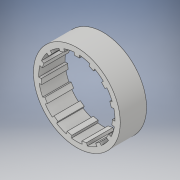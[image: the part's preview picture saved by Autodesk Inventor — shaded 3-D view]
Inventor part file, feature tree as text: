
AUTODESK INVENTOR PART (.ipt)
format: ipt  version: 2018 (Build 220112000, 112)  size: 170,496 bytes
history: native  units: in
note: dims shown in document units (in); Inventor stores cm internally (conversion verified against a paired STEP export)
features: extrude x2, sketch x1, pattern_circular x1
ambient origin geometry x8: Origin, YZ Plane, XZ Plane, XY Plane, X Axis, Y Axis, Z Axis, Center Point
bodies: Solid1 (feature_tree)
feature tree (4):
  sketch  "Sketch1"  dims[d0=1.65in d2=0.05in d3=0.1in d4=0.0275in d5=0.0275in d6=0.5in d7=0.0in d8=0.5in d9=0.0in d10=5.9055in d11=360.0deg]
  extrude  "Extrusion1"  Depth=0.5in
  extrude  "Extrusion2"  Depth=0.5in
  pattern_circular  "Circular Pattern1"  [2 undecoded]
note: 2 required parameter values undecoded (feature->parameter linkage not recoverable at this tier; creation-order binding heuristic only, values carry confidence <= 0.55)
